# Revit family: Estrichüberdecktes Kanalsystem EÜK_Unterflur-Installationskanal_2-zügig
name_source: partatom
category: Generic Models
revit_build: Autodesk Revit 2015 (Build: 20140606_1530(x64)
units: mm (PartAtom-declared; Revit-internal decimal feet)

## types (6) — shared parameters
Manufacturer = OBO Bettermann
Material = Steel, Galvanized
URL = http://www.obo-bettermann.com

## per-type parameters (varying)
| type | GTIN | Manufacturer Art. No. | Size "a" | Size "b" | Width |
| S2 19028 | 4012195089254 | 7400300 | 80 mm  [stored 0.262467 ft] | 110 mm  [stored 0.360892 ft] | 190 mm |
| S2 25028 | 4012195089285 | 7400312 | 110 mm  [stored 0.360892 ft] | 140 mm  [stored 0.459318 ft] | 250 mm  [stored 0.82021 ft] |
| S2 19038 | 4012195089261 | 7400304 | 80 mm  [stored 0.262467 ft] | 110 mm  [stored 0.360892 ft] | 190 mm |
| S2 19048 | 4012195089278 | 7400308 | 80 mm  [stored 0.262467 ft] | 110 mm  [stored 0.360892 ft] | 190 mm |
| S2 25038 | 4012195089315 | 7400316 | 110 mm  [stored 0.360892 ft] | 140 mm  [stored 0.459318 ft] | 250 mm  [stored 0.82021 ft] |
| S2 25048 | 4012195089322 | 7400320 | 110 mm  [stored 0.360892 ft] | 140 mm  [stored 0.459318 ft] | 250 mm  [stored 0.82021 ft] |

note: column(s) folded — value = type name in every type: Article Type

note: [stored X ft] marks values corroborated as IEEE doubles in the binary element streams (Revit-internal decimal feet)

## geometry (parser evidence)
native form markers: Sweep x2
no freeform markers — native parametric forms only
